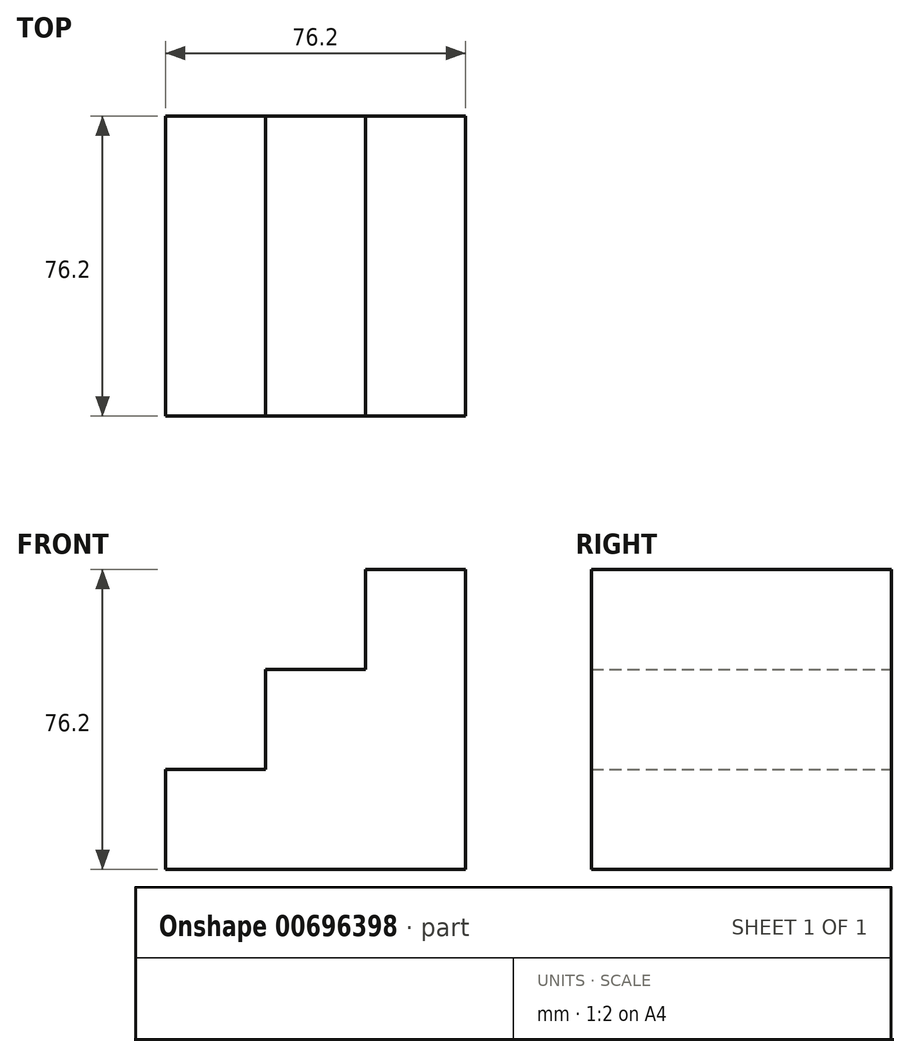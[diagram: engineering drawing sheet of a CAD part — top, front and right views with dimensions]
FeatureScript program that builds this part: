
annotation { "Feature Type Name" : "Feature", "Feature Type Description" : "" }
export const myFeature = defineFeature(function(context is Context, id is Id, definition is map)
    precondition{}
    {
        {
            var Q0;
            Q0=qCreatedBy(makeId("Front.planeOp"),FACE);
            var sketch = newSketch(context, id + "F0", { "sketchPlane" : qUnion([Q0])});
            skLineSegment(sketch, "E0", {"start": v(0, 0) * mm, "end": v(-76.2, 0) * mm});
            skLineSegment(sketch, "E1", {"start": v(0, 0) * mm, "end": v(0, 76.2) * mm});
            skLineSegment(sketch, "E2", {"start": v(0, 76.2) * mm, "end": v(-25.4, 76.2) * mm});
            skLineSegment(sketch, "E3", {"start": v(-25.4, 76.2) * mm, "end": v(-25.4, 50.8) * mm});
            skLineSegment(sketch, "E4", {"start": v(-25.4, 50.8) * mm, "end": v(-50.8, 50.8) * mm});
            skLineSegment(sketch, "E5", {"start": v(-50.8, 50.8) * mm, "end": v(-50.8, 25.4) * mm});
            skLineSegment(sketch, "E6", {"start": v(-50.8, 25.4) * mm, "end": v(-76.2, 25.4) * mm});
            skLineSegment(sketch, "E7", {"start": v(-76.2, 25.4) * mm, "end": v(-76.2, 0) * mm});
            skSolve(sketch);
        }
        {
            var Q0;
            Q0=makeQuery(id+"F0.imprint","IMPRINT",FACE,{"disambiguationData":[TD([[makeQuery(id+"F0.imprint","IMPRINT",EDGE,{"derivedFrom":sQuery(id+"F0.wireOp",EDGE,"E0")}),-1.0]])]});
            extrude(context, id + "F1", {"entities" : qUnion([Q0]), "depth" : 76.2 * mm, "offsetDistance" : 25.4 * mm});
        }
    });
